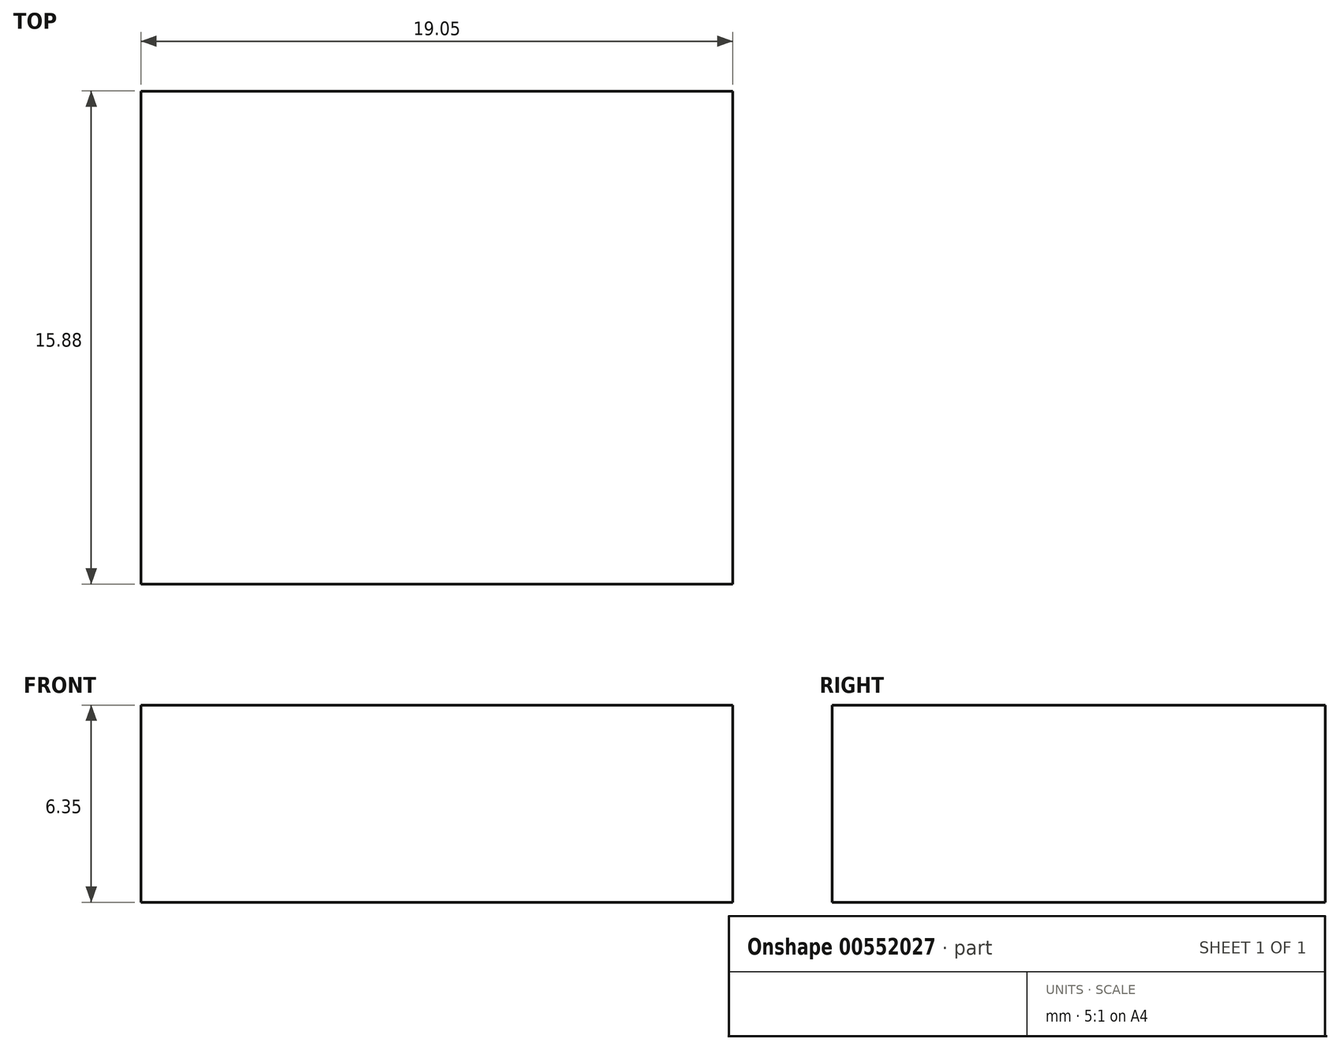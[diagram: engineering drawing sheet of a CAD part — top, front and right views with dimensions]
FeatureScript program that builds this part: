
annotation { "Feature Type Name" : "Feature", "Feature Type Description" : "" }
export const myFeature = defineFeature(function(context is Context, id is Id, definition is map)
    precondition{}
    {
        {
            var Q0;
            Q0=qCreatedBy(makeId("Top.planeOp"),FACE);
            var sketch = newSketch(context, id + "F0", { "sketchPlane" : qUnion([Q0])});
            skLineSegment(sketch, "E0.bottom", {"start": v(0, 0) * mm, "end": v(19.05, 0) * mm});
            skLineSegment(sketch, "E0.top", {"start": v(0, 15.88) * mm, "end": v(19.05, 15.88) * mm});
            skLineSegment(sketch, "E0.left", {"start": v(0, 0) * mm, "end": v(0, 15.88) * mm});
            skLineSegment(sketch, "E0.right", {"start": v(19.05, 0) * mm, "end": v(19.05, 15.88) * mm});
            skSolve(sketch);
        }
        {
            var Q0;
            Q0 = qSketchRegion(id + "F0", true);
            extrude(context, id + "F1", {"entities" : qUnion([Q0]), "depth" : 6.35 * mm, "offsetDistance" : 25.4 * mm});
        }
    });
